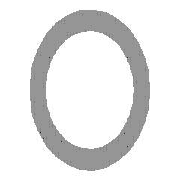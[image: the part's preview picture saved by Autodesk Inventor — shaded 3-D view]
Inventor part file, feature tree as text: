
AUTODESK INVENTOR PART (.ipt)
format: ipt  version: 2013 (Build 170138000, 138)  size: 108,544 bytes
history: native  units: mm (DEFAULTED — no unit token found)
features: other x4, sketch x3, plane x1
ambient origin geometry x8: Origin, YZ Plane, XZ Plane, XY Plane, X Axis, Y Axis, Z Axis, Center Point
bodies: Solid1 (feature_tree), Body (feature_tree)
feature tree (8):
  parser-record x1  (decoder bookkeeping rows leaked as tree rows — omitted from the tree; the rows remain in map.json)
  other  "Driven Length"
  other  "Start plane"
  other  "End plane"
  sketch  "Sketch"  dims[d2=434.975mm d3=0.0mm d4=-0.0mm d5=434.975mm d6=90.0deg d7=434.975mm]
  sketch  "Sketch3"  dims[d0=33.401mm]
  plane  "Work Plane3"
  sketch  "Sketch4"  dims[d1=3.3782mm]
